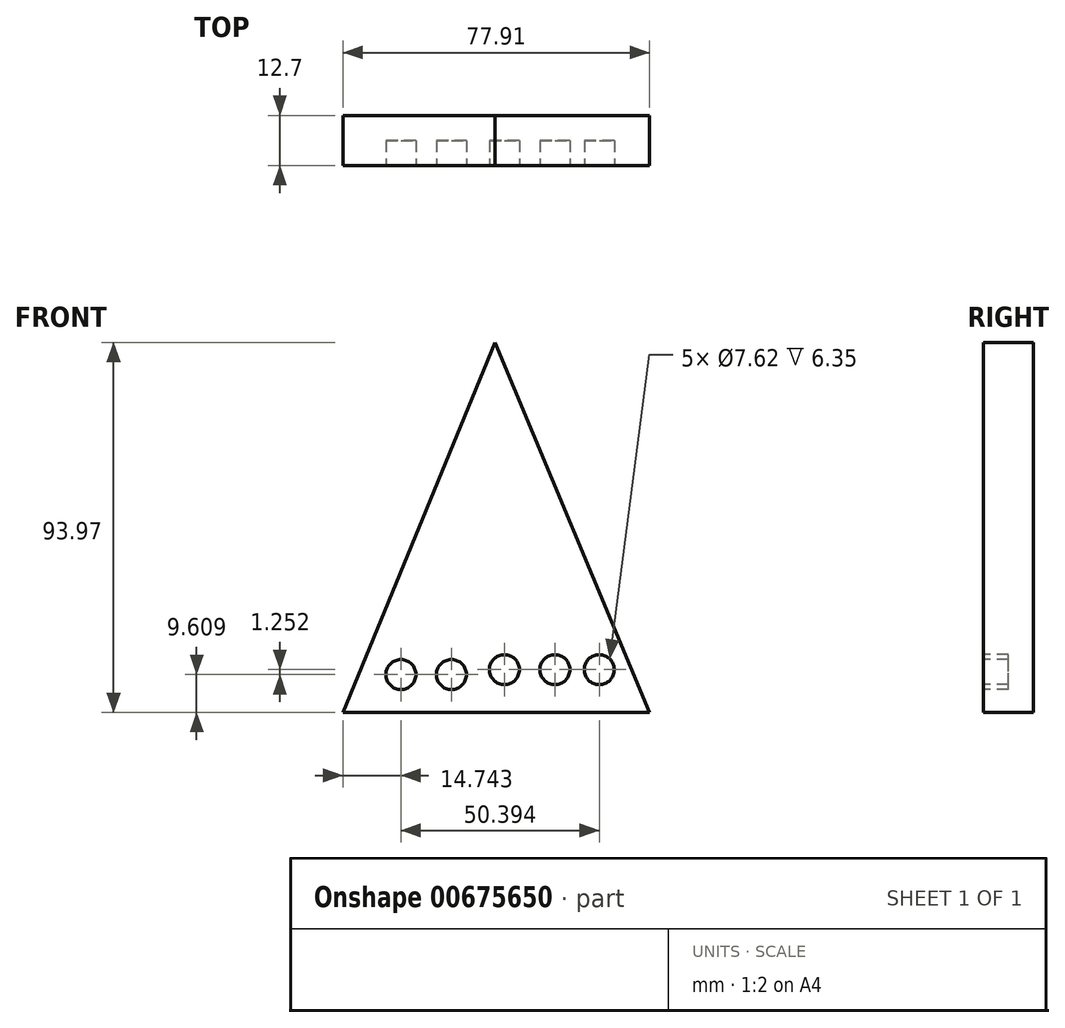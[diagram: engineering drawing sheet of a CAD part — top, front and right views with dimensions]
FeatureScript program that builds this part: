
annotation { "Feature Type Name" : "Feature", "Feature Type Description" : "" }
export const myFeature = defineFeature(function(context is Context, id is Id, definition is map)
    precondition{}
    {
        {
            var Q0;
            Q0=qCreatedBy(makeId("Front.planeOp"),FACE);
            var sketch = newSketch(context, id + "F0", { "sketchPlane" : qUnion([Q0])});
            skLineSegment(sketch, "E0", {"start": v(15, -18.26) * mm, "end": v(-62.91, -18.26) * mm});
            skLineSegment(sketch, "E1", {"start": v(-62.91, -18.26) * mm, "end": v(-24.3, 75.7) * mm});
            skLineSegment(sketch, "E2", {"start": v(-24.3, 75.7) * mm, "end": v(15, -18.26) * mm});
            skSolve(sketch);
        }
        {
            var Q0;
            Q0=makeQuery(id+"F0.imprint","IMPRINT",FACE,{"disambiguationData":[TD([[makeQuery(id+"F0.imprint","IMPRINT",EDGE,{"derivedFrom":sQuery(id+"F0.wireOp",EDGE,"E0")}),-1.0]])]});
            var sketch = newSketch(context, id + "F1", { "sketchPlane" : qUnion([Q0])});
            skSolve(sketch);
        }
        {
            var Q0;
            Q0=makeQuery(id+"F1.imprint","IMPRINT",FACE,{"disambiguationData":[TD([[makeQuery(id+"F1.imprint","IMPRINT",EDGE,{"derivedFrom":makeQuery(id+"F0.imprint","IMPRINT",EDGE,{"derivedFrom":sQuery(id+"F0.wireOp",EDGE,"E0")})}),-1.0]])]});
            extrude(context, id + "F2", {"entities" : qUnion([Q0]), "depth" : 12.7 * mm, "offsetDistance" : 25.4 * mm});
        }
        {
            var Q0;
            Q0=makeQuery(id+"F2.opExtrude","CAP_FACE",FACE,{"disambiguationData":[OSD([sQuery(id+"F0.wireOp",EDGE,"E0"),sQuery(id+"F0.wireOp",EDGE,"E1"),sQuery(id+"F0.wireOp",EDGE,"E2")])],"isStart":false});
            var sketch = newSketch(context, id + "F3", { "sketchPlane" : qUnion([Q0])});
            skCircle(sketch, "E3", {"center": v(-48.17, -8.65) * mm, "radius": 3.81 * mm});
            skCircle(sketch, "E4", {"center": v(-35.33, -8.65) * mm, "radius": 3.81 * mm});
            skCircle(sketch, "E5", {"center": v(-21.87, -7.4) * mm, "radius": 3.81 * mm});
            skCircle(sketch, "E6", {"center": v(-9.04, -7.4) * mm, "radius": 3.81 * mm});
            skCircle(sketch, "E7", {"center": v(2.23, -7.4) * mm, "radius": 3.81 * mm});
            skSolve(sketch);
        }
        {
            var Q0;
            Q0 = qSketchRegion(id + "F3", true);
            extrude(context, id + "F4", {"entities" : qUnion([Q0]), "operationType" : NewBodyOperationType.REMOVE, "oppositeDirection" : true, "depth" : 6.35 * mm, "offsetDistance" : 25.4 * mm});
        }
    });
